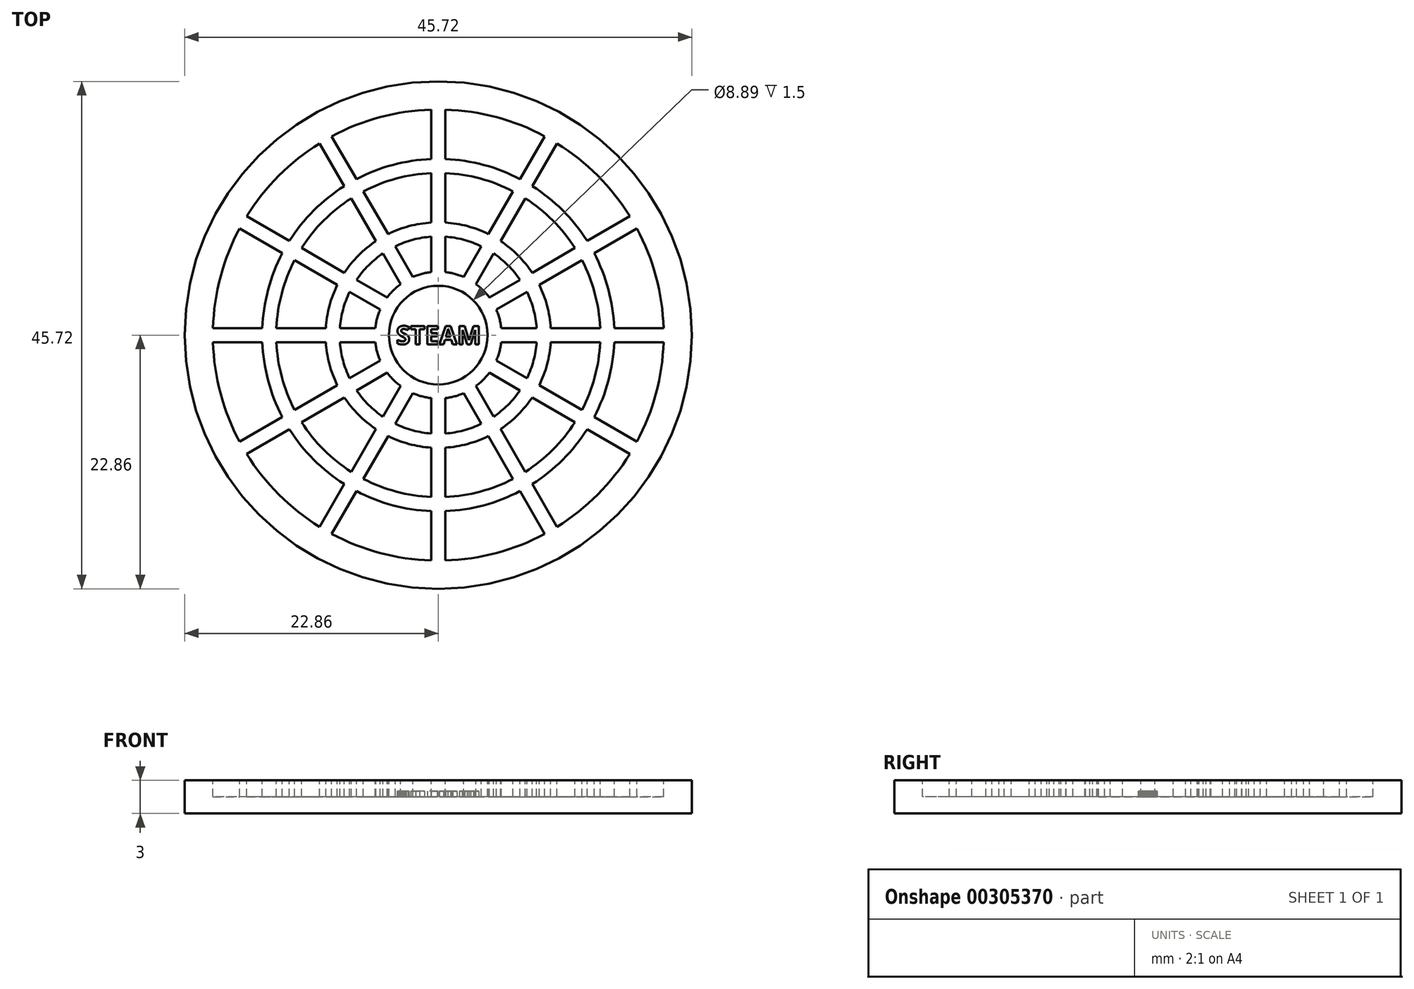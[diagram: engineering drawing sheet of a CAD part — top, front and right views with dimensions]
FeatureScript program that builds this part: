
annotation { "Feature Type Name" : "Feature", "Feature Type Description" : "" }
export const myFeature = defineFeature(function(context is Context, id is Id, definition is map)
    precondition{}
    {
        {
            var Q0;
            Q0=qCreatedBy(makeId("Top.planeOp"),FACE);
            var sketch = newSketch(context, id + "F0", { "sketchPlane" : qUnion([Q0])});
            skCircle(sketch, "E0", {"center": v(0, 0) * mm, "radius": 22.86 * mm});
            skSolve(sketch);
        }
        {
            var Q0;
            Q0 = qSketchRegion(id + "F0", true);
            extrude(context, id + "F1", {"entities" : qUnion([Q0]), "depth" : 3 * mm});
        }
        {
            var Q0;
            Q0=makeQuery(id+"F1.opExtrude","CAP_FACE",FACE,{"disambiguationData":[OSD([sQuery(id+"F0.wireOp",EDGE,"E0")])],"isStart":false});
            var sketch = newSketch(context, id + "F2", { "sketchPlane" : qUnion([Q0])});
            skCircle(sketch, "E1", {"center": v(0, 0) * mm, "radius": 4.45 * mm});
            skPoint(sketch, "E2", {"position": v(0, 5.13) * mm});
            skPoint(sketch, "E2.positionSnap0", {"position": v(0, 5.2) * mm});
            skLineSegment(sketch, "E3", {"start": v(0, 5.13) * mm, "end": v(0, 0) * mm, "construction": true});
            skSolve(sketch);
        }
        {
            var Q0;
            Q0 = qSketchRegion(id + "F2", true);
            extrude(context, id + "F3", {"entities" : qUnion([Q0]), "operationType" : NewBodyOperationType.REMOVE, "oppositeDirection" : true, "depth" : 1.5 * mm});
        }
        {
            var Q0;
            Q0=makeQuery(id+"F1.opExtrude","CAP_FACE",FACE,{"disambiguationData":[OSD([sQuery(id+"F0.wireOp",EDGE,"E0")])],"isStart":false});
            var sketch = newSketch(context, id + "F4", { "sketchPlane" : qUnion([Q0])});
            skCircle(sketch, "E4", {"center": v(0, 0) * mm, "radius": 5.72 * mm});
            skCircle(sketch, "E5", {"center": v(0, 0) * mm, "radius": 8.9 * mm});
            skSolve(sketch);
        }
        {
            var Q0;
            Q0 = qSketchRegion(id + "F4", true);
            extrude(context, id + "F5", {"entities" : qUnion([Q0]), "operationType" : NewBodyOperationType.REMOVE, "oppositeDirection" : true, "depth" : 1.5 * mm});
        }
        {
            var Q0;
            {var subQ0=sQuery(id+"F0.wireOp",EDGE,"E0");Q0=makeQuery(id+"F5.boolean.opBoolean","SPLIT",FACE,{"disambiguationData":[TD([makeQuery(id+"F1.opExtrude","SWEPT_FACE",FACE,{"disambiguationData":[OSD([subQ0])]})])],"derivedFrom":makeQuery(id+"F1.opExtrude","CAP_FACE",FACE,{"disambiguationData":[OSD([subQ0])],"isStart":false})});}
            var sketch = newSketch(context, id + "F6", { "sketchPlane" : qUnion([Q0])});
            skCircle(sketch, "E6", {"center": v(0, 0) * mm, "radius": 10.16 * mm});
            skCircle(sketch, "E7", {"center": v(0, 0) * mm, "radius": 14.6 * mm});
            skSolve(sketch);
        }
        {
            var Q0;
            Q0 = qSketchRegion(id + "F6", true);
            extrude(context, id + "F7", {"entities" : qUnion([Q0]), "operationType" : NewBodyOperationType.REMOVE, "oppositeDirection" : true, "depth" : 1.5 * mm});
        }
        {
            var Q0;
            {var subQ0=sQuery(id+"F0.wireOp",EDGE,"E0");var subQ1=makeQuery(id+"F1.opExtrude","SWEPT_FACE",FACE,{"disambiguationData":[OSD([subQ0])]});Q0=makeQuery(id+"F7.boolean.opBoolean","SPLIT",FACE,{"disambiguationData":[TD([subQ1])],"derivedFrom":makeQuery(id+"F5.boolean.opBoolean","SPLIT",FACE,{"disambiguationData":[TD([subQ1])],"derivedFrom":makeQuery(id+"F1.opExtrude","CAP_FACE",FACE,{"disambiguationData":[OSD([subQ0])],"isStart":false})})});}
            var sketch = newSketch(context, id + "F8", { "sketchPlane" : qUnion([Q0])});
            skCircle(sketch, "E8", {"center": v(0, 0) * mm, "radius": 15.88 * mm});
            skCircle(sketch, "E9", {"center": v(0, 0) * mm, "radius": 20.32 * mm});
            skSolve(sketch);
        }
        {
            var Q0;
            Q0 = qSketchRegion(id + "F8", true);
            extrude(context, id + "F9", {"entities" : qUnion([Q0]), "operationType" : NewBodyOperationType.REMOVE, "oppositeDirection" : true, "depth" : 1.5 * mm});
        }
        {
            var Q0;
            Q0=makeQuery(id+"F9.boolean.opBoolean","COPY",FACE,{"derivedFrom":makeQuery(id+"F9.opExtrude","CAP_FACE",FACE,{"disambiguationData":[OSD([sQuery(id+"F8.wireOp",EDGE,"E8"),sQuery(id+"F8.wireOp",EDGE,"E9")])],"isStart":false})});
            var sketch = newSketch(context, id + "F10", { "sketchPlane" : qUnion([Q0])});
            skLineSegment(sketch, "E10.bottom", {"start": v(-0.64, -4.83) * mm, "end": v(0.63, -4.83) * mm});
            skLineSegment(sketch, "E10.top", {"start": v(-0.64, -21.34) * mm, "end": v(0.64, -21.34) * mm});
            skLineSegment(sketch, "E10.left", {"start": v(-0.64, -4.83) * mm, "end": v(-0.64, -21.34) * mm});
            skLineSegment(sketch, "E10.right", {"start": v(0.63, -4.83) * mm, "end": v(0.64, -21.34) * mm});
            skPoint(sketch, "E11", {"position": v(0, -4.83) * mm});
            skLineSegment(sketch, "E12", {"start": v(0, -21.34) * mm, "end": v(0, -4.83) * mm, "construction": true});
            skLineSegment(sketch, "E13", {"start": v(0, 0) * mm, "end": v(0, -26.5) * mm, "construction": true});
            skLineSegment(sketch, "E14.1.0", {"start": v(2.96, -3.86) * mm, "end": v(11.22, -18.16) * mm});
            skLineSegment(sketch, "E14.1.1", {"start": v(1.86, -4.5) * mm, "end": v(10.12, -18.8) * mm});
            skLineSegment(sketch, "E14.1.2", {"start": v(10.12, -18.8) * mm, "end": v(11.22, -18.16) * mm});
            skLineSegment(sketch, "E14.1.3", {"start": v(1.86, -4.5) * mm, "end": v(2.96, -3.86) * mm});
            skLineSegment(sketch, "E14.2.0", {"start": v(4.5, -1.86) * mm, "end": v(18.8, -10.12) * mm});
            skLineSegment(sketch, "E14.2.1", {"start": v(3.86, -2.96) * mm, "end": v(18.16, -11.22) * mm});
            skLineSegment(sketch, "E14.2.2", {"start": v(18.16, -11.22) * mm, "end": v(18.8, -10.12) * mm});
            skLineSegment(sketch, "E14.2.3", {"start": v(3.86, -2.96) * mm, "end": v(4.5, -1.86) * mm});
            skLineSegment(sketch, "E14.3.0", {"start": v(4.83, 0.63) * mm, "end": v(21.34, 0.63) * mm});
            skLineSegment(sketch, "E14.3.1", {"start": v(4.83, -0.64) * mm, "end": v(21.34, -0.64) * mm});
            skLineSegment(sketch, "E14.3.2", {"start": v(21.34, -0.64) * mm, "end": v(21.34, 0.63) * mm});
            skLineSegment(sketch, "E14.3.3", {"start": v(4.83, -0.64) * mm, "end": v(4.83, 0.63) * mm});
            skLineSegment(sketch, "E14.4.0", {"start": v(3.86, 2.96) * mm, "end": v(18.16, 11.22) * mm});
            skLineSegment(sketch, "E14.4.1", {"start": v(4.5, 1.86) * mm, "end": v(18.8, 10.12) * mm});
            skLineSegment(sketch, "E14.4.2", {"start": v(18.8, 10.12) * mm, "end": v(18.16, 11.22) * mm});
            skLineSegment(sketch, "E14.4.3", {"start": v(4.5, 1.86) * mm, "end": v(3.86, 2.96) * mm});
            skLineSegment(sketch, "E14.5.0", {"start": v(1.86, 4.5) * mm, "end": v(10.12, 18.8) * mm});
            skLineSegment(sketch, "E14.5.1", {"start": v(2.96, 3.86) * mm, "end": v(11.22, 18.16) * mm});
            skLineSegment(sketch, "E14.5.2", {"start": v(11.22, 18.16) * mm, "end": v(10.12, 18.8) * mm});
            skLineSegment(sketch, "E14.5.3", {"start": v(2.96, 3.86) * mm, "end": v(1.86, 4.5) * mm});
            skLineSegment(sketch, "E14.6.0", {"start": v(-0.63, 4.83) * mm, "end": v(-0.63, 21.34) * mm});
            skLineSegment(sketch, "E14.6.1", {"start": v(0.64, 4.83) * mm, "end": v(0.64, 21.34) * mm});
            skLineSegment(sketch, "E14.6.2", {"start": v(0.64, 21.34) * mm, "end": v(-0.63, 21.34) * mm});
            skLineSegment(sketch, "E14.6.3", {"start": v(0.64, 4.83) * mm, "end": v(-0.63, 4.83) * mm});
            skLineSegment(sketch, "E14.7.0", {"start": v(-2.96, 3.86) * mm, "end": v(-11.22, 18.16) * mm});
            skLineSegment(sketch, "E14.7.1", {"start": v(-1.86, 4.5) * mm, "end": v(-10.12, 18.8) * mm});
            skLineSegment(sketch, "E14.7.2", {"start": v(-10.12, 18.8) * mm, "end": v(-11.22, 18.16) * mm});
            skLineSegment(sketch, "E14.7.3", {"start": v(-1.86, 4.5) * mm, "end": v(-2.96, 3.86) * mm});
            skLineSegment(sketch, "E14.8.0", {"start": v(-4.5, 1.86) * mm, "end": v(-18.8, 10.12) * mm});
            skLineSegment(sketch, "E14.8.1", {"start": v(-3.86, 2.96) * mm, "end": v(-18.16, 11.22) * mm});
            skLineSegment(sketch, "E14.8.2", {"start": v(-18.16, 11.22) * mm, "end": v(-18.8, 10.12) * mm});
            skLineSegment(sketch, "E14.8.3", {"start": v(-3.86, 2.96) * mm, "end": v(-4.5, 1.86) * mm});
            skLineSegment(sketch, "E14.9.0", {"start": v(-4.83, -0.63) * mm, "end": v(-21.34, -0.64) * mm});
            skLineSegment(sketch, "E14.9.1", {"start": v(-4.83, 0.64) * mm, "end": v(-21.34, 0.64) * mm});
            skLineSegment(sketch, "E14.9.2", {"start": v(-21.34, 0.64) * mm, "end": v(-21.34, -0.64) * mm});
            skLineSegment(sketch, "E14.9.3", {"start": v(-4.83, 0.64) * mm, "end": v(-4.83, -0.63) * mm});
            skLineSegment(sketch, "E14.10.0", {"start": v(-3.86, -2.96) * mm, "end": v(-18.16, -11.22) * mm});
            skLineSegment(sketch, "E14.10.1", {"start": v(-4.5, -1.86) * mm, "end": v(-18.8, -10.12) * mm});
            skLineSegment(sketch, "E14.10.2", {"start": v(-18.8, -10.12) * mm, "end": v(-18.16, -11.22) * mm});
            skLineSegment(sketch, "E14.10.3", {"start": v(-4.5, -1.86) * mm, "end": v(-3.86, -2.96) * mm});
            skLineSegment(sketch, "E14.11.0", {"start": v(-1.86, -4.5) * mm, "end": v(-10.12, -18.8) * mm});
            skLineSegment(sketch, "E14.11.1", {"start": v(-2.96, -3.86) * mm, "end": v(-11.22, -18.16) * mm});
            skLineSegment(sketch, "E14.11.2", {"start": v(-11.22, -18.16) * mm, "end": v(-10.12, -18.8) * mm});
            skLineSegment(sketch, "E14.11.3", {"start": v(-2.96, -3.86) * mm, "end": v(-1.86, -4.5) * mm});
            skPoint(sketch, "E14.center", {"position": v(0, 0) * mm});
            skSolve(sketch);
        }
        {
            var Q0;
            Q0 = qSketchRegion(id + "F10", true);
            extrude(context, id + "F11", {"entities" : qUnion([Q0]), "operationType" : NewBodyOperationType.ADD, "depth" : 1.5 * mm});
        }
        {
            var Q0;
            Q0=makeQuery(id+"F3.boolean.opBoolean","COPY",FACE,{"derivedFrom":makeQuery(id+"F3.opExtrude","CAP_FACE",FACE,{"disambiguationData":[OSD([sQuery(id+"F2.wireOp",EDGE,"E1")])],"isStart":false})});
            var sketch = newSketch(context, id + "F12", { "sketchPlane" : qUnion([Q0])});
            skText(sketch, "E15", { "text": "STEAM", "fontName": "OpenSans-Bold.ttf"});
            skLineSegment(sketch, "E16", {"start": v(0, 0) * mm, "end": v(0, -2.91) * mm, "construction": true});
            skPoint(sketch, "E17", {"position": v(0, 0) * mm});
            const initialGuessF12  = {"E15": [-0.0038, -0.00083, 1, 0, 0.00166]};
            skSetInitialGuess(sketch, initialGuessF12);
            skSolve(sketch);
        }
        {
            var Q0;
            Q0 = qSketchRegion(id + "F12", true);
            extrude(context, id + "F13", {"entities" : qUnion([Q0]), "operationType" : NewBodyOperationType.ADD, "depth" : .5 * mm});
        }
    });
